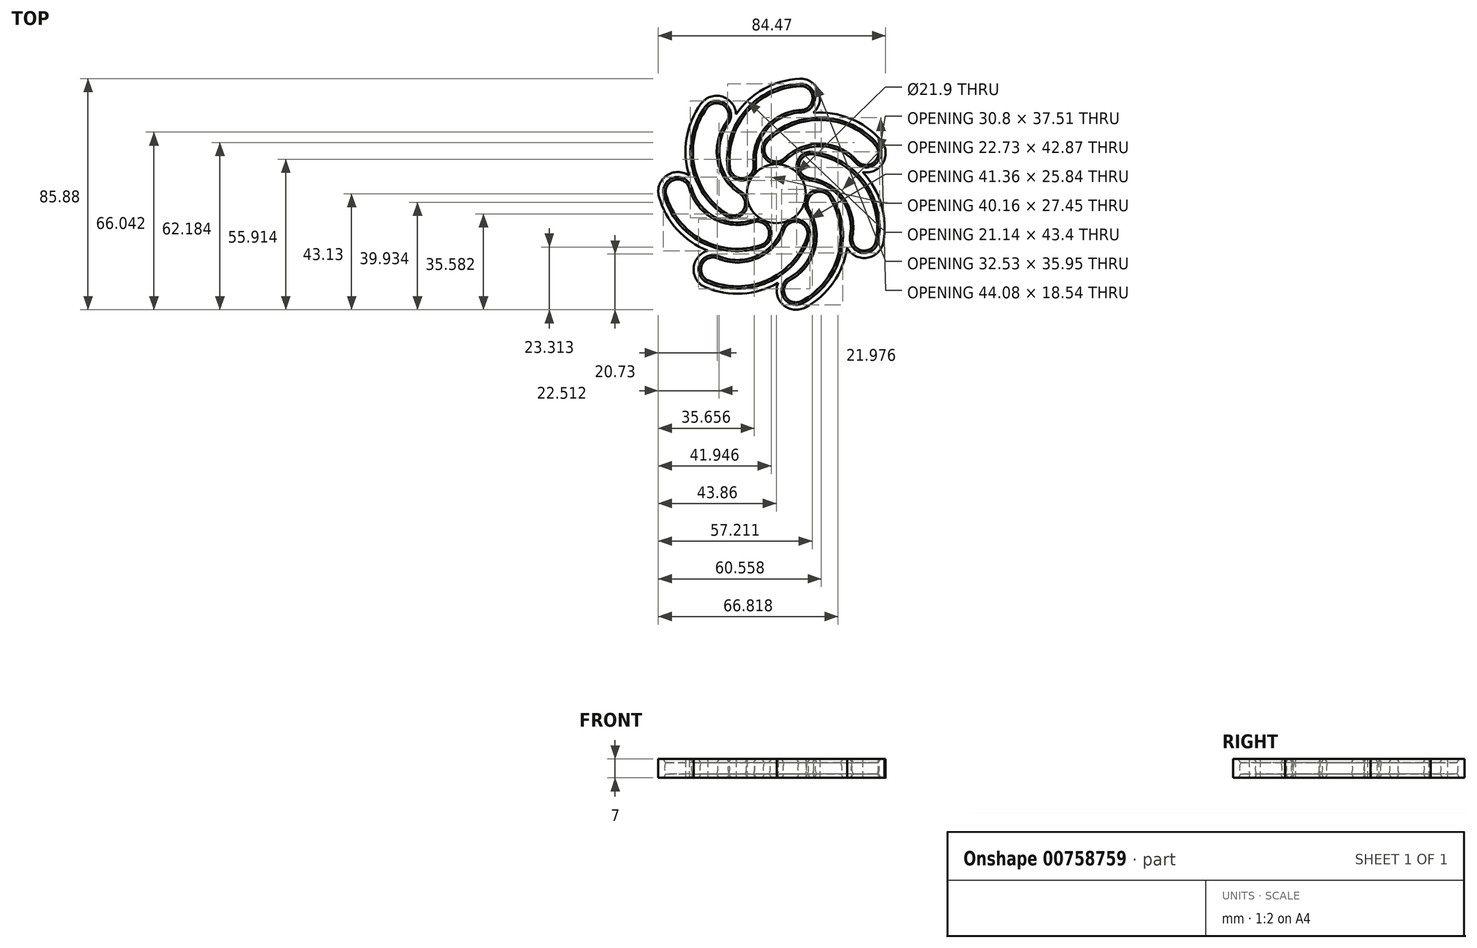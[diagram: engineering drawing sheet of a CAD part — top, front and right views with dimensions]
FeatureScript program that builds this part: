
annotation { "Feature Type Name" : "Feature", "Feature Type Description" : "" }
export const myFeature = defineFeature(function(context is Context, id is Id, definition is map)
    precondition{}
    {
        {
            var Q0;
            Q0=qCreatedBy(makeId("Top.planeOp"),FACE);
            var sketch = newSketch(context, id + "F0", { "sketchPlane" : qUnion([Q0])});
            skArc(sketch, "E0", {"start": v(6.97, 8.45) * mm, "mid": v(0, 10.95) * mm, "end": v(-6.97, 8.45) * mm});
            skPoint(sketch, "E1", {"position": v(0, -24.5) * mm});
            skLineSegment(sketch, "E2", {"start": v(0, 0) * mm, "end": v(0, 16.45) * mm, "construction": true});
            skArc(sketch, "E3", {"start": v(27.98, 10.39) * mm, "mid": v(14.89, 15.76) * mm, "end": v(2.75, 8.49) * mm});
            skArc(sketch, "E4.0", {"start": v(33.4, 15.12) * mm, "mid": v(17, 22.98) * mm, "end": v(0, 16.45) * mm});
            skArc(sketch, "E5.0", {"start": v(38.83, 19.85) * mm, "mid": v(16.37, 30.2) * mm, "end": v(-6.3, 20.3) * mm});
            skArc(sketch, "E6", {"start": v(27.98, 10.39) * mm, "mid": v(38.14, 9.7) * mm, "end": v(38.83, 19.85) * mm});
            skLineSegment(sketch, "E7", {"start": v(-6.97, 8.45) * mm, "end": v(-6.3, 20.3) * mm});
            skArc(sketch, "E8.0", {"start": v(10.47, 12.69) * mm, "mid": v(0, 16.45) * mm, "end": v(-10.47, 12.69) * mm, "construction": true});
            skSolve(sketch);
        }
        {
            var Q0;
            {var subQ4=sQuery(id+"F0.wireOp",EDGE,"PiiM7Q08-lsxY-islm-UEzh-ksM0SnnuY6FK");Q0=makeQuery(id+"F0.imprint","IMPRINT",FACE,{"disambiguationData":[TD([[makeQuery(id+"F0.imprint","IMPRINT",EDGE,{"derivedFrom":subQ4}),-1.0]])]});}
            var Q1;
            Q1=makeQuery(id+"F0.imprint","IMPRINT",FACE,{"disambiguationData":[TD([[makeQuery(id+"F0.imprint","IMPRINT",EDGE,{"derivedFrom":sQuery(id+"F0.wireOp",EDGE,"E0")}),-1.0]])]});
            var Q2;
            {var subQ4=sQuery(id+"F0.wireOp",EDGE,"QqK0a54Q-URX9-TbrE-nkqz-KXdzGL0UVco7");Q2=makeQuery(id+"F0.imprint","IMPRINT",FACE,{"disambiguationData":[TD([[makeQuery(id+"F0.imprint","IMPRINT",EDGE,{"derivedFrom":subQ4}),-1.0]])]});}
            var Q3;
            {var subQ5=sQuery(id+"F0.wireOp",EDGE,"PiiM7Q08-lsxY-islm-UEzh-ksM0SnnuY6FK");Q3=makeQuery(id+"F0.imprint","IMPRINT",FACE,{"disambiguationData":[TD([[makeQuery(id+"F0.imprint","IMPRINT",EDGE,{"derivedFrom":subQ5}),1.0]])]});}
            var Q4;
            {var subQ1=sQuery(id+"F0.wireOp",EDGE,"E5.0");Q4=makeQuery(id+"F0.imprint","IMPRINT",FACE,{"disambiguationData":[TD([[makeQuery(id+"F0.imprint","IMPRINT",EDGE,{"derivedFrom":subQ1}),1.0]])]});}
            extrude(context, id + "F1", {"entities" : qUnion([Q0, Q1, Q2, Q3, Q4]), "endBound" : BoundingType.SYMMETRIC, "depth" : 7 * mm, "offsetDistance" : 25 * mm});
        }
        {
            var Q0;
            Q0=makeQuery(id+"F1.opExtrude","SWEPT_EDGE",EDGE,{"disambiguationData":[OSD([sQuery(id+"F0.wireOp",EDGE,"E3"),sQuery(id+"F0.wireOp",EDGE,"E6")])]});
            var Q1;
            Q1=sQuery(id+"F0.wireOp",VERTEX,"E5.0.start");
            cPlane(context, id + "F2", {"entities" : qUnion([Q0, Q1]), "cplaneType" : CPlaneType.LINE_ANGLE, "offset" : 25 * mm, "angle" : 0 * degree, "width" : 150 * mm, "height" : 150 * mm});
        }
        {
            var Q0;
            Q0=qCreatedBy(id+"F2.planeOp",FACE);
            var sketch = newSketch(context, id + "F3", { "sketchPlane" : qUnion([Q0])});
            skLineSegment(sketch, "E9", {"start": v(35.11, 4.9) * mm, "end": v(35.11, -4.9) * mm});
            skArc(sketch, "E10", {"start": v(35.11, -4.9) * mm, "mid": v(40.01, 0) * mm, "end": v(35.11, 4.9) * mm});
            skArc(sketch, "E11.MirrorCS", {"start": v(35.11, -4.9) * mm, "mid": v(30.21, 0) * mm, "end": v(35.11, 4.9) * mm});
            skSolve(sketch);
        }
        {
            var Q0;
            Q0=makeQuery(id+"F3.imprint","IMPRINT",FACE,{"disambiguationData":[TD([[makeQuery(id+"F3.imprint","IMPRINT",EDGE,{"derivedFrom":sQuery(id+"F3.wireOp",EDGE,"E9")}),1.0]])]});
            var Q1;
            Q1=makeQuery(id+"F3.imprint","IMPRINT",FACE,{"disambiguationData":[TD([[makeQuery(id+"F3.imprint","IMPRINT",EDGE,{"derivedFrom":sQuery(id+"F3.wireOp",EDGE,"E9")}),-1.0]])]});
            var Q2;
            Q2=sQuery(id+"F0.wireOp",EDGE,"E4.0");
            sweep(context, id + "F4", {"operationType" : NewBodyOperationType.REMOVE, "profiles" : qUnion([Q0, Q1]), "path" : qUnion([Q2])});
        }
        {
            var Q0;
            Q0=makeQuery(id+"F3.imprint","IMPRINT",FACE,{"disambiguationData":[TD([[makeQuery(id+"F3.imprint","IMPRINT",EDGE,{"derivedFrom":sQuery(id+"F3.wireOp",EDGE,"E9")}),1.0]])]});
            var Q1;
            Q1=sQuery(id+"F3.wireOp",EDGE,"E9");
            revolve(context, id + "F5", {"operationType" : NewBodyOperationType.REMOVE, "surfaceOperationType" : NewSurfaceOperationType.NEW, "entities" : qUnion([Q0]), "axis" : qUnion([Q1]), "revolveType" : RevolveType.ONE_DIRECTION, "angle" : 180 * degree});
        }
        {
            var Q0;
            Q0=makeQuery(id+"F4.boolean.opBoolean","COPY",FACE,{"derivedFrom":makeQuery(id+"F4.opSweep","CAP_FACE",FACE,{"disambiguationData":[OSD([sQuery(id+"F0.wireOp",VERTEX,"E4.0.end"),sQuery(id+"F3.wireOp",EDGE,"E10"),sQuery(id+"F3.wireOp",EDGE,"E11.MirrorCS")])],"isStart":false})});
            var sketch = newSketch(context, id + "F6", { "sketchPlane" : qUnion([Q0])});
            skLineSegment(sketch, "E12", {"start": v(16.67, 0) * mm, "end": v(6.87, 0) * mm});
            skArc(sketch, "E13", {"start": v(6.87, 0) * mm, "mid": v(11.77, -4.9) * mm, "end": v(16.67, 0) * mm});
            skSolve(sketch);
        }
        {
            var Q0;
            {var subQ1=makeQuery(id+"F4.boolean.opBoolean","INTERSECT",EDGE,{"derivedFrom":[makeQuery(id+"F1.opExtrude","CAP_FACE",FACE,{"disambiguationData":[OSD([sQuery(id+"F0.wireOp",EDGE,"E0"),sQuery(id+"F0.wireOp",EDGE,"Lb8NWhK4-ym9p-KzVv-z8Fr-7k6zUVGv0M9w"),sQuery(id+"F0.wireOp",EDGE,"QqK0a54Q-URX9-TbrE-nkqz-KXdzGL0UVco7"),sQuery(id+"F0.wireOp",EDGE,"E3"),sQuery(id+"F0.wireOp",EDGE,"E5.0"),sQuery(id+"F0.wireOp",EDGE,"E6"),sQuery(id+"F0.wireOp",EDGE,"E7")])],"isStart":true}),makeQuery(id+"F4.opSweep","CAP_FACE",FACE,{"disambiguationData":[OSD([sQuery(id+"F0.wireOp",VERTEX,"I2wmlmdm-DSrS-oub0-GOcV-EtuJTHkaWZzk.end"),sQuery(id+"F3.wireOp",EDGE,"E10"),sQuery(id+"F3.wireOp",EDGE,"E11.MirrorCS")])],"isStart":false})]});Q0=makeQuery(id+"F6.imprint","IMPRINT",FACE,{"disambiguationData":[TD([[makeQuery(id+"F6.imprint","IMPRINT",EDGE,{"derivedFrom":subQ1}),-1.0]])]});}
            var Q1;
            {var subQ0=sQuery(id+"F6.wireOp",EDGE,"E12");Q1=makeQuery(id+"F6.imprint","IMPRINT",FACE,{"disambiguationData":[TD([[makeQuery(id+"F6.imprint","IMPRINT",EDGE,{"derivedFrom":subQ0}),1.0]])]});}
            var Q2;
            Q2=sQuery(id+"F6.wireOp",EDGE,"E12");
            revolve(context, id + "F7", {"operationType" : NewBodyOperationType.REMOVE, "surfaceOperationType" : NewSurfaceOperationType.NEW, "entities" : qUnion([Q0, Q1]), "axis" : qUnion([Q2]), "revolveType" : RevolveType.FULL, "oppositeDirection" : true});
        }
        {
            var Q0;
            Q0=qCreatedBy(makeId("Front.planeOp"),FACE);
            var sketch = newSketch(context, id + "F8", { "sketchPlane" : qUnion([Q0])});
            skLineSegment(sketch, "E14", {"start": v(0, -9.37) * mm, "end": v(0, 10.86) * mm, "construction": true});
            skSolve(sketch);
        }
        {
            var Q0;
            Q0=makeQuery(id+"F1.opExtrude","SWEPT_BODY",BODY,{"disambiguationData":[OSD([sQuery(id+"F0.wireOp",EDGE,"E0"),sQuery(id+"F0.wireOp",EDGE,"Lb8NWhK4-ym9p-KzVv-z8Fr-7k6zUVGv0M9w"),sQuery(id+"F0.wireOp",EDGE,"QqK0a54Q-URX9-TbrE-nkqz-KXdzGL0UVco7"),sQuery(id+"F0.wireOp",EDGE,"E3"),sQuery(id+"F0.wireOp",EDGE,"E5.0"),sQuery(id+"F0.wireOp",EDGE,"E6"),sQuery(id+"F0.wireOp",EDGE,"E7")])]});
            var Q1;
            Q1=sQuery(id+"F8.wireOp",EDGE,"E14");
            circularPattern(context, id + "F9", {"operationType" : NewBodyOperationType.ADD, "entities" : qUnion([Q0]), "axis" : qUnion([Q1]), "angle" : 360 * degree, "instanceCount" : 7, "equalSpace" : true});
        }
        {
            var Q0;
            Q0=makeQuery(id+"F9.opPattern","COPY",EDGE,{"derivedFrom":makeQuery(id+"F4.boolean.opBoolean","INTERSECT",EDGE,{"disambiguationData":[OD(1.0)],"derivedFrom":[makeQuery(id+"F1.opExtrude","CAP_FACE",FACE,{"disambiguationData":[OSD([sQuery(id+"F0.wireOp",EDGE,"E0"),sQuery(id+"F0.wireOp",EDGE,"E3"),sQuery(id+"F0.wireOp",EDGE,"E5.0"),sQuery(id+"F0.wireOp",EDGE,"E6"),sQuery(id+"F0.wireOp",EDGE,"E7")])],"isStart":false}),makeQuery(id+"F4.opSweep","SWEPT_FACE",FACE,{"disambiguationData":[OSD([sQuery(id+"F0.wireOp",EDGE,"E4.0"),sQuery(id+"F3.wireOp",EDGE,"E10"),sQuery(id+"F3.wireOp",EDGE,"E11.MirrorCS")])]})]}),"instanceName":"3"});
            var Q1;
            Q1=makeQuery(id+"F9.opPattern","COPY",EDGE,{"derivedFrom":makeQuery(id+"F4.boolean.opBoolean","INTERSECT",EDGE,{"disambiguationData":[OD(0.0)],"derivedFrom":[makeQuery(id+"F1.opExtrude","CAP_FACE",FACE,{"disambiguationData":[OSD([sQuery(id+"F0.wireOp",EDGE,"E0"),sQuery(id+"F0.wireOp",EDGE,"E3"),sQuery(id+"F0.wireOp",EDGE,"E5.0"),sQuery(id+"F0.wireOp",EDGE,"E6"),sQuery(id+"F0.wireOp",EDGE,"E7")])],"isStart":false}),makeQuery(id+"F4.opSweep","SWEPT_FACE",FACE,{"disambiguationData":[OSD([sQuery(id+"F0.wireOp",EDGE,"E4.0"),sQuery(id+"F3.wireOp",EDGE,"E10"),sQuery(id+"F3.wireOp",EDGE,"E11.MirrorCS")])]})]}),"instanceName":"4"});
            var Q2;
            Q2=makeQuery(id+"F9.opPattern","COPY",EDGE,{"derivedFrom":makeQuery(id+"F4.boolean.opBoolean","INTERSECT",EDGE,{"disambiguationData":[OD(1.0)],"derivedFrom":[makeQuery(id+"F1.opExtrude","CAP_FACE",FACE,{"disambiguationData":[OSD([sQuery(id+"F0.wireOp",EDGE,"E0"),sQuery(id+"F0.wireOp",EDGE,"E3"),sQuery(id+"F0.wireOp",EDGE,"E5.0"),sQuery(id+"F0.wireOp",EDGE,"E6"),sQuery(id+"F0.wireOp",EDGE,"E7")])],"isStart":false}),makeQuery(id+"F4.opSweep","SWEPT_FACE",FACE,{"disambiguationData":[OSD([sQuery(id+"F0.wireOp",EDGE,"E4.0"),sQuery(id+"F3.wireOp",EDGE,"E10"),sQuery(id+"F3.wireOp",EDGE,"E11.MirrorCS")])]})]}),"instanceName":"5"});
            var Q3;
            Q3=makeQuery(id+"F9.opPattern","COPY",EDGE,{"derivedFrom":makeQuery(id+"F4.boolean.opBoolean","INTERSECT",EDGE,{"disambiguationData":[OD(0.0)],"derivedFrom":[makeQuery(id+"F1.opExtrude","CAP_FACE",FACE,{"disambiguationData":[OSD([sQuery(id+"F0.wireOp",EDGE,"E0"),sQuery(id+"F0.wireOp",EDGE,"E3"),sQuery(id+"F0.wireOp",EDGE,"E5.0"),sQuery(id+"F0.wireOp",EDGE,"E6"),sQuery(id+"F0.wireOp",EDGE,"E7")])],"isStart":false}),makeQuery(id+"F4.opSweep","SWEPT_FACE",FACE,{"disambiguationData":[OSD([sQuery(id+"F0.wireOp",EDGE,"E4.0"),sQuery(id+"F3.wireOp",EDGE,"E10"),sQuery(id+"F3.wireOp",EDGE,"E11.MirrorCS")])]})]}),"instanceName":"6"});
            var Q4;
            Q4=makeQuery(id+"F4.boolean.opBoolean","INTERSECT",EDGE,{"disambiguationData":[OD(0.0)],"derivedFrom":[makeQuery(id+"F1.opExtrude","CAP_FACE",FACE,{"disambiguationData":[OSD([sQuery(id+"F0.wireOp",EDGE,"E0"),sQuery(id+"F0.wireOp",EDGE,"E3"),sQuery(id+"F0.wireOp",EDGE,"E5.0"),sQuery(id+"F0.wireOp",EDGE,"E6"),sQuery(id+"F0.wireOp",EDGE,"E7")])],"isStart":false}),makeQuery(id+"F4.opSweep","SWEPT_FACE",FACE,{"disambiguationData":[OSD([sQuery(id+"F0.wireOp",EDGE,"E4.0"),sQuery(id+"F3.wireOp",EDGE,"E10"),sQuery(id+"F3.wireOp",EDGE,"E11.MirrorCS")])]})]});
            var Q5;
            Q5=makeQuery(id+"F9.opPattern","COPY",EDGE,{"derivedFrom":makeQuery(id+"F4.boolean.opBoolean","INTERSECT",EDGE,{"disambiguationData":[OD(0.0)],"derivedFrom":[makeQuery(id+"F1.opExtrude","CAP_FACE",FACE,{"disambiguationData":[OSD([sQuery(id+"F0.wireOp",EDGE,"E0"),sQuery(id+"F0.wireOp",EDGE,"E3"),sQuery(id+"F0.wireOp",EDGE,"E5.0"),sQuery(id+"F0.wireOp",EDGE,"E6"),sQuery(id+"F0.wireOp",EDGE,"E7")])],"isStart":false}),makeQuery(id+"F4.opSweep","SWEPT_FACE",FACE,{"disambiguationData":[OSD([sQuery(id+"F0.wireOp",EDGE,"E4.0"),sQuery(id+"F3.wireOp",EDGE,"E10"),sQuery(id+"F3.wireOp",EDGE,"E11.MirrorCS")])]})]}),"instanceName":"1"});
            var Q6;
            Q6=makeQuery(id+"F9.opPattern","COPY",EDGE,{"derivedFrom":makeQuery(id+"F4.boolean.opBoolean","INTERSECT",EDGE,{"disambiguationData":[OD(0.0)],"derivedFrom":[makeQuery(id+"F1.opExtrude","CAP_FACE",FACE,{"disambiguationData":[OSD([sQuery(id+"F0.wireOp",EDGE,"E0"),sQuery(id+"F0.wireOp",EDGE,"E3"),sQuery(id+"F0.wireOp",EDGE,"E5.0"),sQuery(id+"F0.wireOp",EDGE,"E6"),sQuery(id+"F0.wireOp",EDGE,"E7")])],"isStart":false}),makeQuery(id+"F4.opSweep","SWEPT_FACE",FACE,{"disambiguationData":[OSD([sQuery(id+"F0.wireOp",EDGE,"E4.0"),sQuery(id+"F3.wireOp",EDGE,"E10"),sQuery(id+"F3.wireOp",EDGE,"E11.MirrorCS")])]})]}),"instanceName":"2"});
            var Q7;
            Q7=makeQuery(id+"F9.opPattern","COPY",EDGE,{"derivedFrom":makeQuery(id+"F4.boolean.opBoolean","INTERSECT",EDGE,{"disambiguationData":[OD(1.0)],"derivedFrom":[makeQuery(id+"F1.opExtrude","CAP_FACE",FACE,{"disambiguationData":[OSD([sQuery(id+"F0.wireOp",EDGE,"E0"),sQuery(id+"F0.wireOp",EDGE,"E3"),sQuery(id+"F0.wireOp",EDGE,"E5.0"),sQuery(id+"F0.wireOp",EDGE,"E6"),sQuery(id+"F0.wireOp",EDGE,"E7")])],"isStart":true}),makeQuery(id+"F4.opSweep","SWEPT_FACE",FACE,{"disambiguationData":[OSD([sQuery(id+"F0.wireOp",EDGE,"E4.0"),sQuery(id+"F3.wireOp",EDGE,"E10"),sQuery(id+"F3.wireOp",EDGE,"E11.MirrorCS")])]})]}),"instanceName":"4"});
            var Q8;
            Q8=makeQuery(id+"F9.opPattern","COPY",EDGE,{"derivedFrom":makeQuery(id+"F4.boolean.opBoolean","INTERSECT",EDGE,{"disambiguationData":[OD(0.0)],"derivedFrom":[makeQuery(id+"F1.opExtrude","CAP_FACE",FACE,{"disambiguationData":[OSD([sQuery(id+"F0.wireOp",EDGE,"E0"),sQuery(id+"F0.wireOp",EDGE,"E3"),sQuery(id+"F0.wireOp",EDGE,"E5.0"),sQuery(id+"F0.wireOp",EDGE,"E6"),sQuery(id+"F0.wireOp",EDGE,"E7")])],"isStart":true}),makeQuery(id+"F4.opSweep","SWEPT_FACE",FACE,{"disambiguationData":[OSD([sQuery(id+"F0.wireOp",EDGE,"E4.0"),sQuery(id+"F3.wireOp",EDGE,"E10"),sQuery(id+"F3.wireOp",EDGE,"E11.MirrorCS")])]})]}),"instanceName":"5"});
            var Q9;
            Q9=makeQuery(id+"F9.opPattern","COPY",EDGE,{"derivedFrom":makeQuery(id+"F4.boolean.opBoolean","INTERSECT",EDGE,{"disambiguationData":[OD(0.0)],"derivedFrom":[makeQuery(id+"F1.opExtrude","CAP_FACE",FACE,{"disambiguationData":[OSD([sQuery(id+"F0.wireOp",EDGE,"E0"),sQuery(id+"F0.wireOp",EDGE,"E3"),sQuery(id+"F0.wireOp",EDGE,"E5.0"),sQuery(id+"F0.wireOp",EDGE,"E6"),sQuery(id+"F0.wireOp",EDGE,"E7")])],"isStart":true}),makeQuery(id+"F4.opSweep","SWEPT_FACE",FACE,{"disambiguationData":[OSD([sQuery(id+"F0.wireOp",EDGE,"E4.0"),sQuery(id+"F3.wireOp",EDGE,"E10"),sQuery(id+"F3.wireOp",EDGE,"E11.MirrorCS")])]})]}),"instanceName":"6"});
            var Q10;
            Q10=makeQuery(id+"F4.boolean.opBoolean","INTERSECT",EDGE,{"disambiguationData":[OD(0.0)],"derivedFrom":[makeQuery(id+"F1.opExtrude","CAP_FACE",FACE,{"disambiguationData":[OSD([sQuery(id+"F0.wireOp",EDGE,"E0"),sQuery(id+"F0.wireOp",EDGE,"E3"),sQuery(id+"F0.wireOp",EDGE,"E5.0"),sQuery(id+"F0.wireOp",EDGE,"E6"),sQuery(id+"F0.wireOp",EDGE,"E7")])],"isStart":true}),makeQuery(id+"F4.opSweep","SWEPT_FACE",FACE,{"disambiguationData":[OSD([sQuery(id+"F0.wireOp",EDGE,"E4.0"),sQuery(id+"F3.wireOp",EDGE,"E10"),sQuery(id+"F3.wireOp",EDGE,"E11.MirrorCS")])]})]});
            var Q11;
            Q11=makeQuery(id+"F9.opPattern","COPY",EDGE,{"derivedFrom":makeQuery(id+"F4.boolean.opBoolean","INTERSECT",EDGE,{"disambiguationData":[OD(0.0)],"derivedFrom":[makeQuery(id+"F1.opExtrude","CAP_FACE",FACE,{"disambiguationData":[OSD([sQuery(id+"F0.wireOp",EDGE,"E0"),sQuery(id+"F0.wireOp",EDGE,"E3"),sQuery(id+"F0.wireOp",EDGE,"E5.0"),sQuery(id+"F0.wireOp",EDGE,"E6"),sQuery(id+"F0.wireOp",EDGE,"E7")])],"isStart":true}),makeQuery(id+"F4.opSweep","SWEPT_FACE",FACE,{"disambiguationData":[OSD([sQuery(id+"F0.wireOp",EDGE,"E4.0"),sQuery(id+"F3.wireOp",EDGE,"E10"),sQuery(id+"F3.wireOp",EDGE,"E11.MirrorCS")])]})]}),"instanceName":"1"});
            var Q12;
            Q12=makeQuery(id+"F9.opPattern","COPY",EDGE,{"derivedFrom":makeQuery(id+"F4.boolean.opBoolean","INTERSECT",EDGE,{"disambiguationData":[OD(0.0)],"derivedFrom":[makeQuery(id+"F1.opExtrude","CAP_FACE",FACE,{"disambiguationData":[OSD([sQuery(id+"F0.wireOp",EDGE,"E0"),sQuery(id+"F0.wireOp",EDGE,"E3"),sQuery(id+"F0.wireOp",EDGE,"E5.0"),sQuery(id+"F0.wireOp",EDGE,"E6"),sQuery(id+"F0.wireOp",EDGE,"E7")])],"isStart":true}),makeQuery(id+"F4.opSweep","SWEPT_FACE",FACE,{"disambiguationData":[OSD([sQuery(id+"F0.wireOp",EDGE,"E4.0"),sQuery(id+"F3.wireOp",EDGE,"E10"),sQuery(id+"F3.wireOp",EDGE,"E11.MirrorCS")])]})]}),"instanceName":"2"});
            var Q13;
            Q13=makeQuery(id+"F9.opPattern","COPY",EDGE,{"derivedFrom":makeQuery(id+"F4.boolean.opBoolean","INTERSECT",EDGE,{"disambiguationData":[OD(0.0)],"derivedFrom":[makeQuery(id+"F1.opExtrude","CAP_FACE",FACE,{"disambiguationData":[OSD([sQuery(id+"F0.wireOp",EDGE,"E0"),sQuery(id+"F0.wireOp",EDGE,"E3"),sQuery(id+"F0.wireOp",EDGE,"E5.0"),sQuery(id+"F0.wireOp",EDGE,"E6"),sQuery(id+"F0.wireOp",EDGE,"E7")])],"isStart":true}),makeQuery(id+"F4.opSweep","SWEPT_FACE",FACE,{"disambiguationData":[OSD([sQuery(id+"F0.wireOp",EDGE,"E4.0"),sQuery(id+"F3.wireOp",EDGE,"E10"),sQuery(id+"F3.wireOp",EDGE,"E11.MirrorCS")])]})]}),"instanceName":"3"});
            chamfer(context, id + "F10", {"entities" : qUnion([Q0, Q1, Q2, Q3, Q4, Q5, Q6, Q7, Q8, Q9, Q10, Q11, Q12, Q13]), "width" : 1 * mm, "tangentPropagation" : true});
        }
    });
